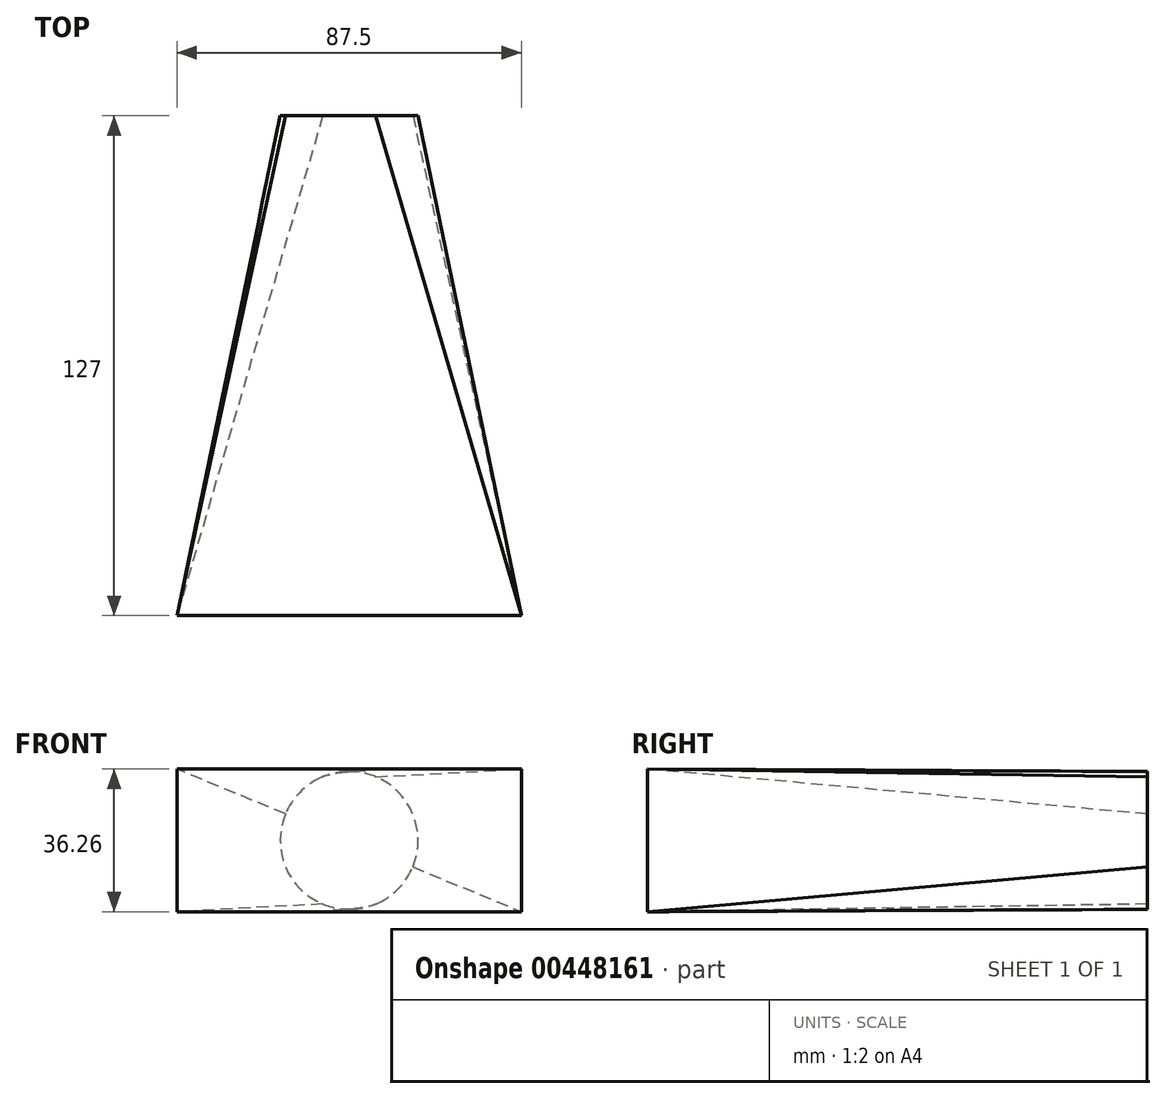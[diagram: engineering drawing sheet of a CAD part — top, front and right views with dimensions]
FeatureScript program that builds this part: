
annotation { "Feature Type Name" : "Feature", "Feature Type Description" : "" }
export const myFeature = defineFeature(function(context is Context, id is Id, definition is map)
    precondition{}
    {
        {
            var Q0;
            Q0=qCreatedBy(makeId("Front.planeOp"),FACE);
            var sketch = newSketch(context, id + "F0", { "sketchPlane" : qUnion([Q0])});
            skCircle(sketch, "E0", {"center": v(0, 0) * mm, "radius": 17.5 * mm});
            skSolve(sketch);
        }
        {
            var Q0;
            Q0=qCreatedBy(makeId("Front.planeOp"),FACE);
            cPlane(context, id + "F1", {"entities" : qUnion([Q0]), "cplaneType" : CPlaneType.OFFSET, "offset" : 127 * mm, "width" : 152.4 * mm, "height" : 152.4 * mm});
        }
        {
            var Q0;
            Q0=qCreatedBy(id+"F1.planeOp",FACE);
            var sketch = newSketch(context, id + "F2", { "sketchPlane" : qUnion([Q0])});
            skLineSegment(sketch, "E1.bottom", {"start": v(-43.75, 18.13) * mm, "end": v(43.75, 18.13) * mm});
            skLineSegment(sketch, "E1.top", {"start": v(-43.75, -18.13) * mm, "end": v(43.75, -18.13) * mm});
            skLineSegment(sketch, "E1.left", {"start": v(-43.75, 18.13) * mm, "end": v(-43.75, -18.13) * mm});
            skLineSegment(sketch, "E1.right", {"start": v(43.75, 18.13) * mm, "end": v(43.75, -18.13) * mm});
            skPoint(sketch, "E1.middle", {"position": v(0, 0) * mm});
            skSolve(sketch);
        }
        {
            var Q0;
            Q0=makeQuery(id+"F0.imprint","IMPRINT",FACE,{"disambiguationData":[TD([[makeQuery(id+"F0.imprint","IMPRINT",EDGE,{"derivedFrom":sQuery(id+"F0.wireOp",EDGE,"E0")}),1.0]])]});
            var Q1;
            Q1=makeQuery(id+"F2.imprint","IMPRINT",FACE,{"disambiguationData":[TD([[makeQuery(id+"F2.imprint","IMPRINT",EDGE,{"derivedFrom":sQuery(id+"F2.wireOp",EDGE,"E1.bottom")}),-1.0]])]});
            loft(context, id + "F3", {"sheetProfilesArray" : [{ "sheetProfileEntities" : qUnion([Q0]) }, { "sheetProfileEntities" : qUnion([Q1]) }]});
        }
    });
